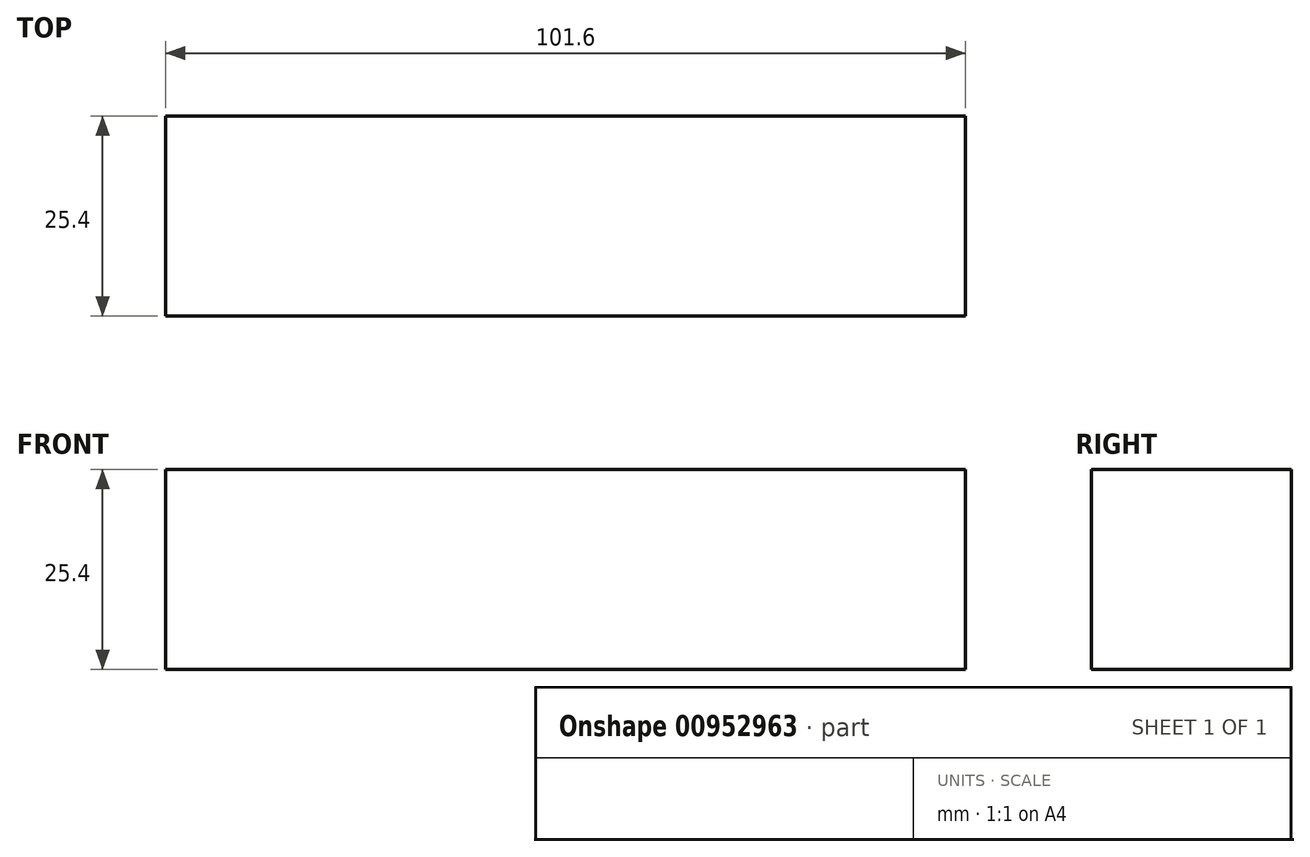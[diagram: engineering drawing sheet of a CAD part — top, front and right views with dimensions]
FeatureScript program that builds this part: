
annotation { "Feature Type Name" : "Feature", "Feature Type Description" : "" }
export const myFeature = defineFeature(function(context is Context, id is Id, definition is map)
    precondition{}
    {
        {
            var Q0;
            Q0=qCreatedBy(makeId("Top.planeOp"),FACE);
            var sketch = newSketch(context, id + "F0", { "sketchPlane" : qUnion([Q0])});
            skLineSegment(sketch, "E0.bottom", {"start": v(-50.8, 12.7) * mm, "end": v(50.8, 12.7) * mm});
            skLineSegment(sketch, "E0.top", {"start": v(-50.8, -12.7) * mm, "end": v(50.8, -12.7) * mm});
            skLineSegment(sketch, "E0.left", {"start": v(-50.8, 12.7) * mm, "end": v(-50.8, -12.7) * mm});
            skLineSegment(sketch, "E0.right", {"start": v(50.8, 12.7) * mm, "end": v(50.8, -12.7) * mm});
            skSolve(sketch);
        }
        {
            var Q0;
            Q0 = qSketchRegion(id + "F0", true);
            extrude(context, id + "F1", {"entities" : qUnion([Q0]), "depth" : 25.4 * mm, "offsetDistance" : 25.4 * mm});
        }
        {
            var Q0;
            Q0=qCreatedBy(makeId("Right.planeOp"),FACE);
            var sketch = newSketch(context, id + "F2", { "sketchPlane" : qUnion([Q0])});
            skLineSegment(sketch, "E1", {"start": v(3.42, 15.44) * mm, "end": v(53.83, 67.4) * mm});
            skSolve(sketch);
        }
    });
